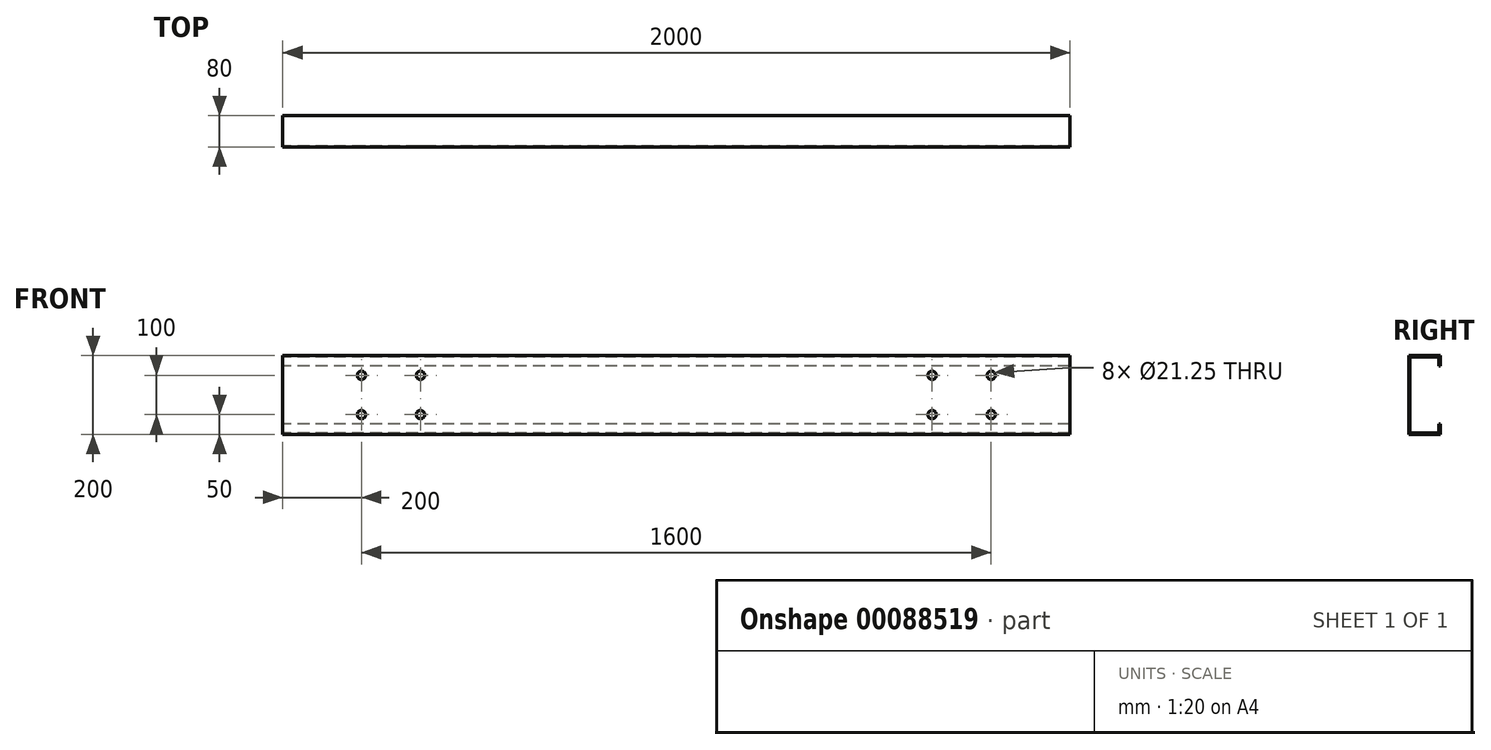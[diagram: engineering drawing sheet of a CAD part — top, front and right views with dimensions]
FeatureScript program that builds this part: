
annotation { "Feature Type Name" : "Feature", "Feature Type Description" : "" }
export const myFeature = defineFeature(function(context is Context, id is Id, definition is map)
    precondition{}
    {
        {
            var Q0;
            Q0=qCreatedBy(makeId("Right.planeOp"),FACE);
            var sketch = newSketch(context, id + "F0", { "sketchPlane" : qUnion([Q0])});
            skLineSegment(sketch, "E0", {"start": v(0, 0) * mm, "end": v(0, 100) * mm});
            skLineSegment(sketch, "E1", {"start": v(0, 100) * mm, "end": v(80, 100) * mm});
            skLineSegment(sketch, "E2", {"start": v(80, 100) * mm, "end": v(80, 73.98) * mm});
            skLineSegment(sketch, "E3", {"start": v(80, 73.98) * mm, "end": v(77, 73.98) * mm});
            skLineSegment(sketch, "E4", {"start": v(77, 73.98) * mm, "end": v(77, 97) * mm});
            skLineSegment(sketch, "E5", {"start": v(77, 97) * mm, "end": v(3, 97) * mm});
            skLineSegment(sketch, "E6", {"start": v(3, 97) * mm, "end": v(3, 0) * mm});
            skLineSegment(sketch, "E7", {"start": v(0, 0) * mm, "end": v(197.71, 0) * mm, "construction": true});
            skLineSegment(sketch, "E8.MirrorCS", {"start": v(80, -73.98) * mm, "end": v(77, -73.98) * mm});
            skLineSegment(sketch, "E9.MirrorCS", {"start": v(0, 0) * mm, "end": v(0, -100) * mm});
            skLineSegment(sketch, "E10.MirrorCS", {"start": v(0, -100) * mm, "end": v(80, -100) * mm});
            skLineSegment(sketch, "E11.MirrorCS", {"start": v(3, -97) * mm, "end": v(3, 0) * mm});
            skLineSegment(sketch, "E12.MirrorCS", {"start": v(80, -100) * mm, "end": v(80, -73.98) * mm});
            skLineSegment(sketch, "E13.MirrorCS", {"start": v(77, -73.98) * mm, "end": v(77, -97) * mm});
            skLineSegment(sketch, "E14.MirrorCS", {"start": v(77, -97) * mm, "end": v(3, -97) * mm});
            skSolve(sketch);
        }
        {
            var Q0;
            Q0=makeQuery(id+"F0.imprint","IMPRINT",FACE,{"disambiguationData":[TD([[makeQuery(id+"F0.imprint","IMPRINT",EDGE,{"derivedFrom":sQuery(id+"F0.wireOp",EDGE,"E0")}),-1.0]])]});
            extrude(context, id + "F1", {"entities" : qUnion([Q0]), "depth" : 2000 * mm});
        }
        {
            var Q0;
            Q0=makeQuery(id+"F1.opExtrude","SWEPT_FACE",FACE,{"disambiguationData":[OSD([sQuery(id+"F0.wireOp",EDGE,"E0"),sQuery(id+"F0.wireOp",EDGE,"E9.MirrorCS")])]});
            var sketch = newSketch(context, id + "F2", { "sketchPlane" : qUnion([Q0])});
            skCircle(sketch, "E15", {"center": v(200, 50) * mm, "radius": 10.63 * mm});
            skCircle(sketch, "E16.0.1.0", {"center": v(200, -50) * mm, "radius": 10.63 * mm});
            skCircle(sketch, "E16.1.0.0", {"center": v(350, 50) * mm, "radius": 10.63 * mm});
            skCircle(sketch, "E16.1.1.0", {"center": v(350, -50) * mm, "radius": 10.63 * mm});
            skLineSegment(sketch, "E16.direction1", {"start": v(200, 50) * mm, "end": v(350, 50) * mm, "construction": true});
            skLineSegment(sketch, "E16.direction2", {"start": v(200, 50) * mm, "end": v(200, -50) * mm, "construction": true});
            skSolve(sketch);
        }
        {
            var Q0;
            Q0 = qSketchRegion(id + "F2", true);
            extrude(context, id + "F3", {"entities" : qUnion([Q0]), "operationType" : NewBodyOperationType.REMOVE, "oppositeDirection" : true, "depth" : 25 * mm});
        }
        {
            var Q0;
            Q0=makeQuery(id+"F1.opExtrude","SWEPT_FACE",FACE,{"disambiguationData":[OSD([sQuery(id+"F0.wireOp",EDGE,"E0"),sQuery(id+"F0.wireOp",EDGE,"E9.MirrorCS")])]});
            var sketch = newSketch(context, id + "F4", { "sketchPlane" : qUnion([Q0])});
            skCircle(sketch, "E17", {"center": v(1650, 50) * mm, "radius": 10.63 * mm});
            skCircle(sketch, "E18.0.1.0", {"center": v(1650, -50) * mm, "radius": 10.63 * mm});
            skCircle(sketch, "E18.1.0.0", {"center": v(1800, 50) * mm, "radius": 10.63 * mm});
            skCircle(sketch, "E18.1.1.0", {"center": v(1800, -50) * mm, "radius": 10.63 * mm});
            skLineSegment(sketch, "E18.direction1", {"start": v(1650, 50) * mm, "end": v(1800, 50) * mm, "construction": true});
            skLineSegment(sketch, "E18.direction2", {"start": v(1650, 50) * mm, "end": v(1650, -50) * mm, "construction": true});
            skSolve(sketch);
        }
        {
            var Q0;
            Q0=makeQuery(id+"F4.imprint","IMPRINT",FACE,{"disambiguationData":[TD([[makeQuery(id+"F4.imprint","IMPRINT",EDGE,{"derivedFrom":sQuery(id+"F4.wireOp",EDGE,"E17")}),1.0]])]});
            var Q1;
            Q1=makeQuery(id+"F4.imprint","IMPRINT",FACE,{"disambiguationData":[TD([[makeQuery(id+"F4.imprint","IMPRINT",EDGE,{"derivedFrom":sQuery(id+"F4.wireOp",EDGE,"E18.0.1.0")}),1.0]])]});
            var Q2;
            Q2=makeQuery(id+"F4.imprint","IMPRINT",FACE,{"disambiguationData":[TD([[makeQuery(id+"F4.imprint","IMPRINT",EDGE,{"derivedFrom":sQuery(id+"F4.wireOp",EDGE,"E18.1.0.0")}),1.0]])]});
            var Q3;
            Q3=makeQuery(id+"F4.imprint","IMPRINT",FACE,{"disambiguationData":[TD([[makeQuery(id+"F4.imprint","IMPRINT",EDGE,{"derivedFrom":sQuery(id+"F4.wireOp",EDGE,"E18.1.1.0")}),1.0]])]});
            extrude(context, id + "F5", {"entities" : qUnion([Q0, Q1, Q2, Q3]), "operationType" : NewBodyOperationType.REMOVE, "oppositeDirection" : true, "depth" : 25 * mm});
        }
    });
